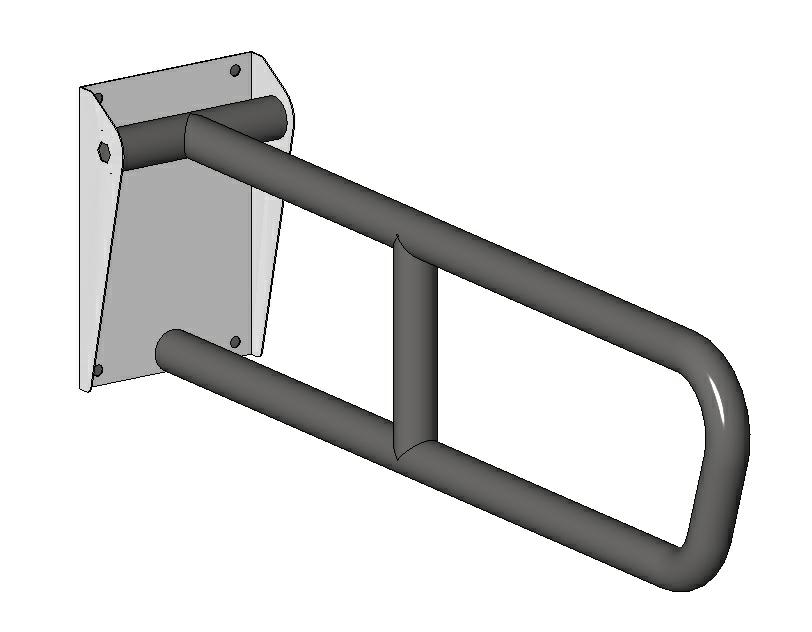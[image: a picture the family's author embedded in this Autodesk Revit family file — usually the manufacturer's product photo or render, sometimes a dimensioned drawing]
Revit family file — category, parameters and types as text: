
# Revit family: GS3207300
name_source: partatom
category: Generic Models
revit_build: Autodesk Revit 2016 (Build: 20150220_1215(x64)
units: mm (PartAtom-declared; Revit-internal decimal feet)

## family parameters
Always vertical = Yes
Can host rebar = No
Cut with Voids When Loaded = No
Host = Wall
Part Type = Normal
Room Calculation Point = No
Round Connector Dimension = Use Diameter
Shared = No

## types (1)
- 150 x 730 x 228
    Assembly Code = E2010
    Base Material = Aluminum
    Description = Barra de apoyo abatible acero inoxidable tipo AISI 304 con tubo de 1 ¼” de diámetro de con flanges marca Wasser
    Height = 1000 mm  [stored 3.28084 ft]
    Manufacturer = CHC
    Material = Stainless Steel, Polished
    Model = GS3207300
    Type Image = GS3207300.jpg
    URL = www.grupochc.cl

note: [stored X ft] marks values corroborated as IEEE doubles in the binary element streams (Revit-internal decimal feet)

## geometry (parser evidence)
native form markers: Sweep x2
no freeform markers — native parametric forms only
